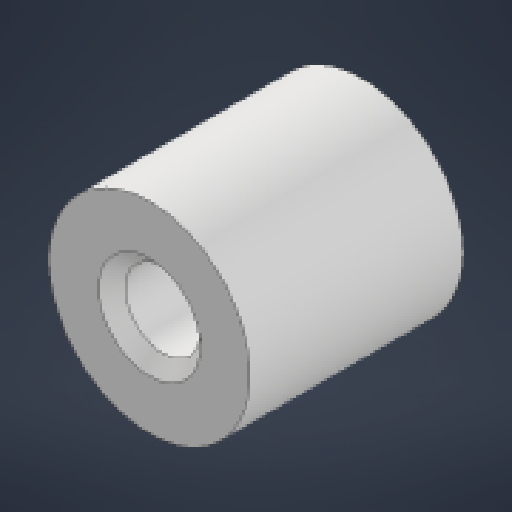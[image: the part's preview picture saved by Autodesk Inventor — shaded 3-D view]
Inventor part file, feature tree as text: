
AUTODESK INVENTOR PART (.ipt)
format: ipt  version: 2024.1 (Build 281209000, 209)  size: 134,656 bytes
history: native  units: in
note: dims shown in document units (in); Inventor stores cm internally (conversion verified against a paired STEP export)
features: extrude x1, chamfer x1, sketch x1
ambient origin geometry x8: Origin, YZ Plane, XZ Plane, XY Plane, X Axis, Y Axis, Z Axis, Center Point
bodies: Solid1 (feature_tree)
feature tree (3):
  extrude  "Extrusion1"  Depth=0.5in
  chamfer  "Chamfer1"  Distance=0.5in
  sketch  "Sketch1"  dims[d0=0.1772in d1=0.4724in d2=0.5in d3=0.0in d4=0.0312in d5=0.125in d6=45.0deg]
